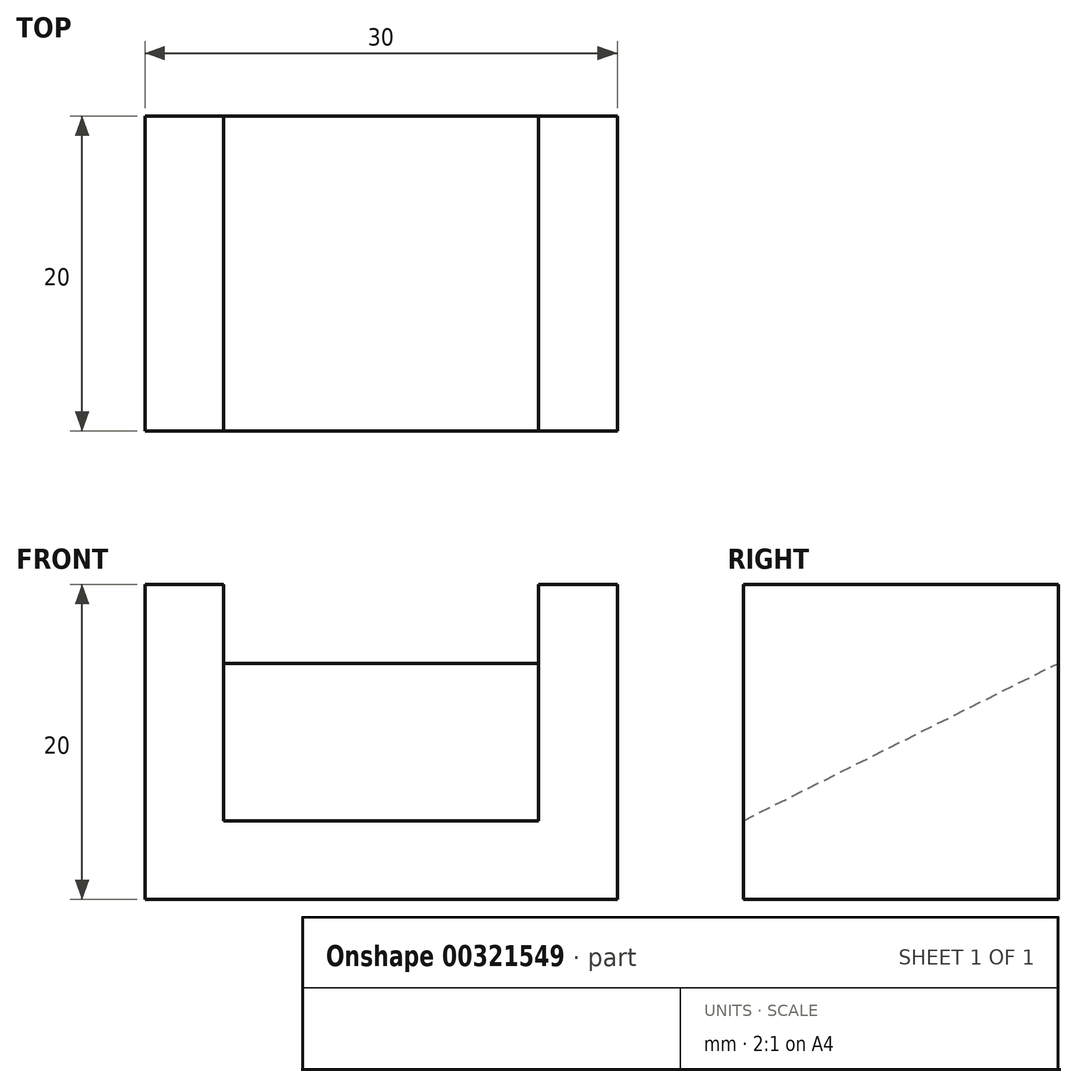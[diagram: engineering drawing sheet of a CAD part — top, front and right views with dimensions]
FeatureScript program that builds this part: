
annotation { "Feature Type Name" : "Feature", "Feature Type Description" : "" }
export const myFeature = defineFeature(function(context is Context, id is Id, definition is map)
    precondition{}
    {
        {
            var Q0;
            Q0=qCreatedBy(makeId("Right.planeOp"),FACE);
            var sketch = newSketch(context, id + "F0", { "sketchPlane" : qUnion([Q0])});
            skLineSegment(sketch, "E0.bottom", {"start": v(0, 0) * mm, "end": v(20, 0) * mm});
            skLineSegment(sketch, "E0.top", {"start": v(0, -20) * mm, "end": v(20, -20) * mm});
            skLineSegment(sketch, "E0.left", {"start": v(0, 0) * mm, "end": v(0, -20) * mm});
            skLineSegment(sketch, "E0.right", {"start": v(20, 0) * mm, "end": v(20, -20) * mm});
            skSolve(sketch);
        }
        {
            var Q0;
            Q0=makeQuery(id+"F0.imprint","IMPRINT",FACE,{"disambiguationData":[TD([[makeQuery(id+"F0.imprint","IMPRINT",EDGE,{"derivedFrom":sQuery(id+"F0.wireOp",EDGE,"E0.bottom")}),-1.0]])]});
            extrude(context, id + "F1", {"entities" : qUnion([Q0]), "depth" : 30 * mm});
        }
        {
            var Q0;
            Q0=makeQuery(id+"F1.opExtrude","CAP_FACE",FACE,{"disambiguationData":[OSD([sQuery(id+"F0.wireOp",EDGE,"E0.bottom"),sQuery(id+"F0.wireOp",EDGE,"E0.top"),sQuery(id+"F0.wireOp",EDGE,"E0.left"),sQuery(id+"F0.wireOp",EDGE,"E0.right")])],"isStart":false});
            var sketch = newSketch(context, id + "F2", { "sketchPlane" : qUnion([Q0])});
            skLineSegment(sketch, "E1", {"start": v(20, 0) * mm, "end": v(0, 0) * mm});
            skLineSegment(sketch, "E2", {"start": v(0, 0) * mm, "end": v(0, -15) * mm});
            skLineSegment(sketch, "E3", {"start": v(0, -15) * mm, "end": v(20, -5) * mm});
            skLineSegment(sketch, "E4", {"start": v(20, -5) * mm, "end": v(20, 0) * mm});
            skSolve(sketch);
        }
        {
            var Q0;
            Q0=makeQuery(id+"F2.imprint","IMPRINT",FACE,{"disambiguationData":[TD([[makeQuery(id+"F2.imprint","IMPRINT",EDGE,{"derivedFrom":sQuery(id+"F2.wireOp",EDGE,"E1")}),-1.0]])]});
            extrude(context, id + "F3", {"entities" : qUnion([Q0]), "operationType" : NewBodyOperationType.REMOVE, "oppositeDirection" : true, "depth" : 25 * mm, "hasSecondDirection" : true, "secondDirectionOppositeDirection" : true, "secondDirectionDepth" : 5 * mm});
        }
    });
